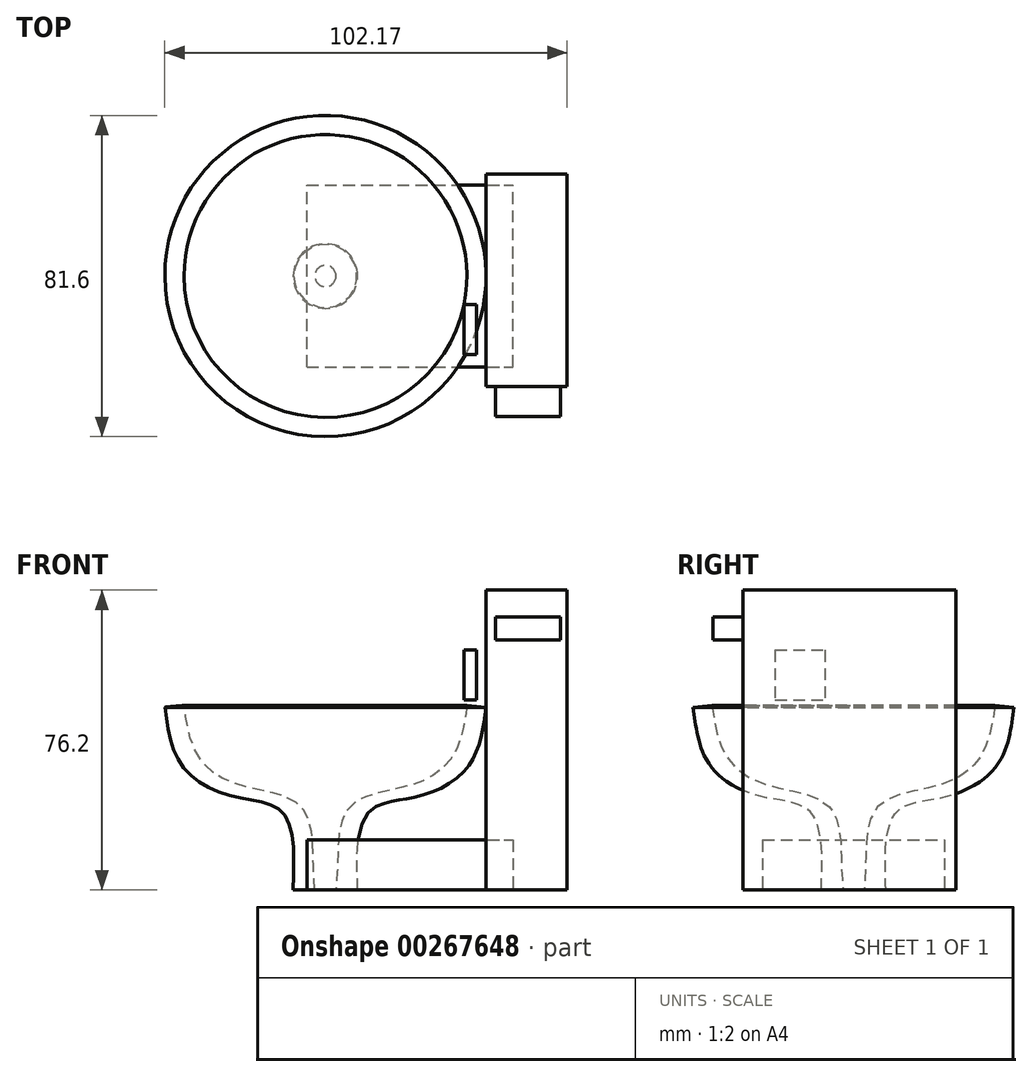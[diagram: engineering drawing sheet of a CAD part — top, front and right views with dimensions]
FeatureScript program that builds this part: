
annotation { "Feature Type Name" : "Feature", "Feature Type Description" : "" }
export const myFeature = defineFeature(function(context is Context, id is Id, definition is map)
    precondition{}
    {
        {
            var Q0;
            Q0=qCreatedBy(makeId("Top.planeOp"),FACE);
            var sketch = newSketch(context, id + "F0", { "sketchPlane" : qUnion([Q0])});
            skLineSegment(sketch, "E0.bottom", {"start": v(0, 25.95) * mm, "end": v(20.57, 25.95) * mm});
            skLineSegment(sketch, "E0.top", {"start": v(0, -28.1) * mm, "end": v(20.57, -28.1) * mm});
            skLineSegment(sketch, "E0.left", {"start": v(0, 25.95) * mm, "end": v(0, -28.1) * mm});
            skLineSegment(sketch, "E0.right", {"start": v(20.57, 25.95) * mm, "end": v(20.57, -28.1) * mm});
            skSolve(sketch);
        }
        {
            var Q0;
            Q0 = qSketchRegion(id + "F0", true);
            extrude(context, id + "F1", {"entities" : qUnion([Q0]), "depth" : 76.2 * mm});
        }
        {
            var Q0;
            Q0=qCreatedBy(makeId("Front.planeOp"),FACE);
            var sketch = newSketch(context, id + "F2", { "sketchPlane" : qUnion([Q0])});
            skFitSpline(sketch, "E1", {"points": [v(0, 46.46) * mm, v(-4.23, 31.86) * mm, v(-17.14, 23.81) * mm, v(-29.84, 19.8) * mm, v(-32.6, 0) * mm], "startDerivative": vector(-8.73, -64.82) * mm, "endDerivative": vector(3.06, -86.6) * mm});
            skFitSpline(sketch, "E2", {"points": [v(-38.1, 0) * mm, v(-37.68, 8.15) * mm, v(-34.5, 21.27) * mm, v(-18, 26.99) * mm, v(-8.04, 34.82) * mm, v(-4.87, 46.88) * mm], "startDerivative": vector(3.12, 45.27) * mm, "endDerivative": vector(9.36, 64.76) * mm});
            skLineSegment(sketch, "E3", {"start": v(-38.1, 0) * mm, "end": v(-32.6, 0) * mm});
            skLineSegment(sketch, "E4", {"start": v(-4.87, 46.88) * mm, "end": v(0, 46.46) * mm});
            skSolve(sketch);
        }
        {
            var Q0;
            Q0=qCreatedBy(makeId("Front.planeOp"),FACE);
            var sketch = newSketch(context, id + "F3", { "sketchPlane" : qUnion([Q0])});
            skLineSegment(sketch, "E5.bottom", {"start": v(0, 0) * mm, "end": v(-40.8, 0) * mm});
            skLineSegment(sketch, "E5.top", {"start": v(0, 51.07) * mm, "end": v(-40.8, 51.07) * mm});
            skLineSegment(sketch, "E5.left", {"start": v(0, 0) * mm, "end": v(0, 51.07) * mm});
            skLineSegment(sketch, "E5.right", {"start": v(-40.8, 0) * mm, "end": v(-40.8, 51.07) * mm});
            skSolve(sketch);
        }
        {
            var Q0;
            Q0=makeQuery(id+"F2.imprint","IMPRINT",FACE,{"disambiguationData":[TD([[makeQuery(id+"F2.imprint","IMPRINT",EDGE,{"derivedFrom":sQuery(id+"F2.wireOp",EDGE,"E1")}),-1.0]])]});
            var Q1;
            Q1=sQuery(id+"F3.wireOp",EDGE,"E5.right");
            revolve(context, id + "F4", {"entities" : qUnion([Q0]), "axis" : qUnion([Q1]), "revolveType" : RevolveType.FULL});
        }
        {
            var Q0;
            Q0=makeQuery(id+"F1.opExtrude","SWEPT_FACE",FACE,{"disambiguationData":[OSD([sQuery(id+"F0.wireOp",EDGE,"E0.top")])]});
            var sketch = newSketch(context, id + "F5", { "sketchPlane" : qUnion([Q0])});
            skLineSegment(sketch, "E6.bottom", {"start": v(2.46, 69.4) * mm, "end": v(18.87, 69.4) * mm});
            skLineSegment(sketch, "E6.top", {"start": v(2.46, 63.6) * mm, "end": v(18.87, 63.6) * mm});
            skLineSegment(sketch, "E6.left", {"start": v(2.46, 69.4) * mm, "end": v(2.46, 63.6) * mm});
            skLineSegment(sketch, "E6.right", {"start": v(18.87, 69.4) * mm, "end": v(18.87, 63.6) * mm});
            skSolve(sketch);
        }
        {
            var Q0;
            Q0 = qSketchRegion(id + "F5", true);
            extrude(context, id + "F6", {"entities" : qUnion([Q0]), "operationType" : NewBodyOperationType.ADD, "depth" : 7.62 * mm});
        }
        {
            var Q0;
            Q0=qCreatedBy(makeId("Top.planeOp"),FACE);
            var sketch = newSketch(context, id + "F7", { "sketchPlane" : qUnion([Q0])});
            skLineSegment(sketch, "E7.bottom", {"start": v(-45.52, -23.1) * mm, "end": v(6.9, -23.1) * mm});
            skLineSegment(sketch, "E7.top", {"start": v(-45.52, 23.1) * mm, "end": v(6.9, 23.1) * mm});
            skLineSegment(sketch, "E7.left", {"start": v(-45.52, -23.1) * mm, "end": v(-45.52, 23.1) * mm});
            skLineSegment(sketch, "E7.right", {"start": v(6.9, -23.1) * mm, "end": v(6.9, 23.1) * mm});
            skPoint(sketch, "E7.middle", {"position": v(-19.3, 0) * mm});
            skSolve(sketch);
        }
        {
            var Q0;
            Q0 = qSketchRegion(id + "F7", true);
            extrude(context, id + "F8", {"entities" : qUnion([Q0]), "depth" : 12.7 * mm});
        }
        {
            var Q0;
            Q0=makeQuery(id+"F8.opExtrude","CAP_FACE",FACE,{"disambiguationData":[OSD([sQuery(id+"F7.wireOp",EDGE,"E7.bottom"),sQuery(id+"F7.wireOp",EDGE,"E7.top"),sQuery(id+"F7.wireOp",EDGE,"E7.left"),sQuery(id+"F7.wireOp",EDGE,"E7.right")])],"isStart":false});
            cPlane(context, id + "F9", {"entities" : qUnion([Q0]), "cplaneType" : CPlaneType.OFFSET, "offset" : 35.56 * mm, "width" : 152.4 * mm, "height" : 152.4 * mm});
        }
        {
            var Q0;
            Q0=qCreatedBy(id+"F9.planeOp",FACE);
            var sketch = newSketch(context, id + "F10", { "sketchPlane" : qUnion([Q0])});
            skLineSegment(sketch, "E8.bottom", {"start": v(-5.64, -5.47) * mm, "end": v(-2.45, -5.47) * mm});
            skLineSegment(sketch, "E8.top", {"start": v(-5.64, 5.47) * mm, "end": v(-2.45, 5.47) * mm});
            skLineSegment(sketch, "E8.left", {"start": v(-5.64, -5.47) * mm, "end": v(-5.64, 5.47) * mm});
            skLineSegment(sketch, "E8.right", {"start": v(-2.45, -5.47) * mm, "end": v(-2.45, 5.47) * mm});
            skPoint(sketch, "E8.middle", {"position": v(-4.04, 0) * mm});
            skSolve(sketch);
        }
        {
            var Q0;
            Q0 = qSketchRegion(id + "F10", true);
            extrude(context, id + "F11", {"entities" : qUnion([Q0]), "depth" : 12.7 * mm});
        }
        {
            var Q0;
            Q0=makeQuery(id+"F11.opExtrude","SWEPT_FACE",FACE,{"disambiguationData":[OSD([sQuery(id+"F10.wireOp",EDGE,"E8.top")])]});
            extrude(context, id + "F12", {"entities" : qUnion([Q0]), "operationType" : NewBodyOperationType.ADD, "oppositeDirection" : true, "depth" : 25.4 * mm});
        }
        {
            var Q0;
            Q0=makeQuery(id+"F11.opExtrude","SWEPT_FACE",FACE,{"disambiguationData":[OSD([sQuery(id+"F10.wireOp",EDGE,"E8.top")])]});
            extrude(context, id + "F13", {"entities" : qUnion([Q0]), "operationType" : NewBodyOperationType.REMOVE, "oppositeDirection" : true, "depth" : 12.7 * mm});
        }
    });
